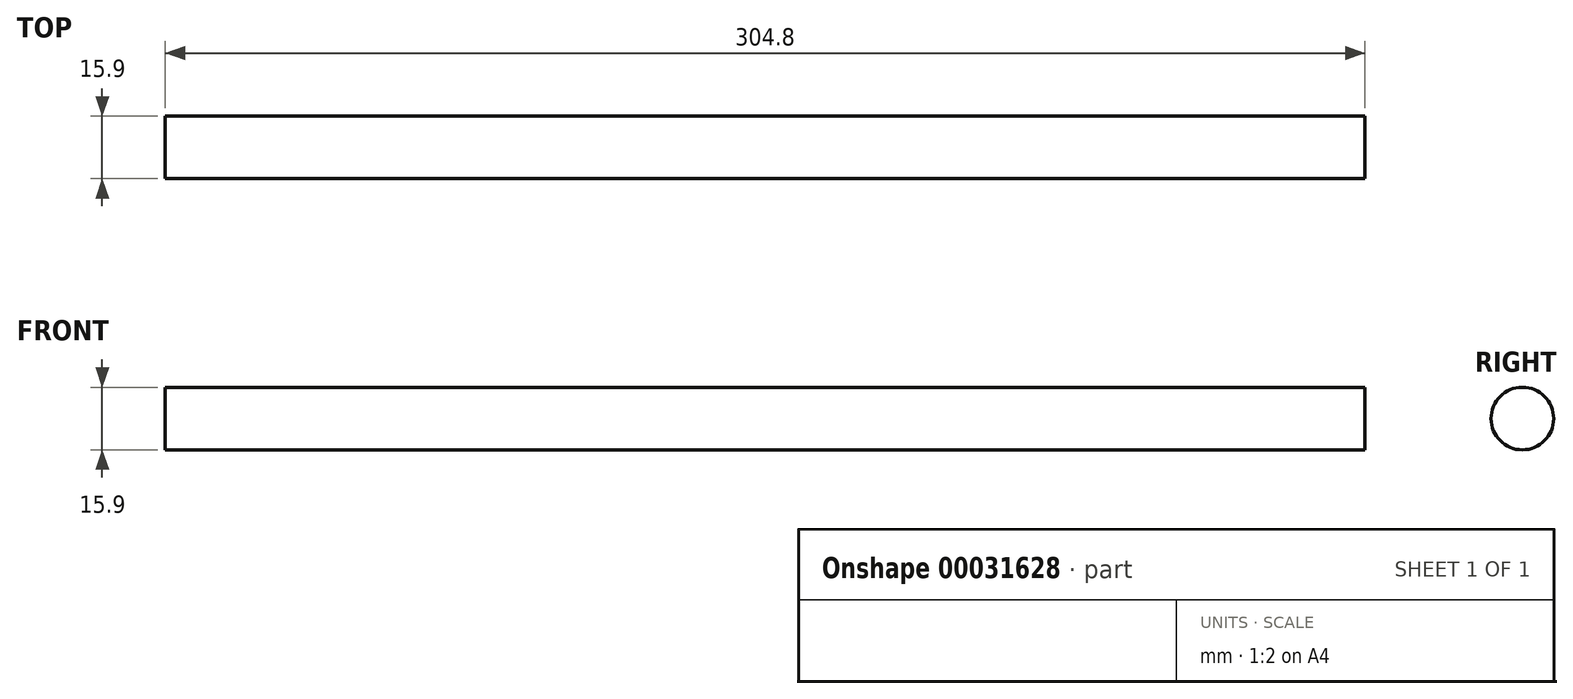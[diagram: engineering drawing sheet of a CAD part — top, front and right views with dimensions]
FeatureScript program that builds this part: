
annotation { "Feature Type Name" : "Feature", "Feature Type Description" : "" }
export const myFeature = defineFeature(function(context is Context, id is Id, definition is map)
    precondition{}
    {
        {
            var Q0;
            Q0=qCreatedBy(makeId("Right.planeOp"),FACE);
            var sketch = newSketch(context, id + "F0", { "sketchPlane" : qUnion([Q0])});
            skCircle(sketch, "E0", {"center": v(0, 0) * mm, "radius": 7.95 * mm});
            skSolve(sketch);
        }
        {
            var Q0;
            Q0=makeQuery(id+"F0.imprint","IMPRINT",FACE,{"disambiguationData":[TD([[makeQuery(id+"F0.imprint","IMPRINT",EDGE,{"derivedFrom":sQuery(id+"F0.wireOp",EDGE,"E0")}),1.0]])]});
            extrude(context, id + "F1", {"entities" : qUnion([Q0]), "depth" : 304.8 * mm});
        }
    });
